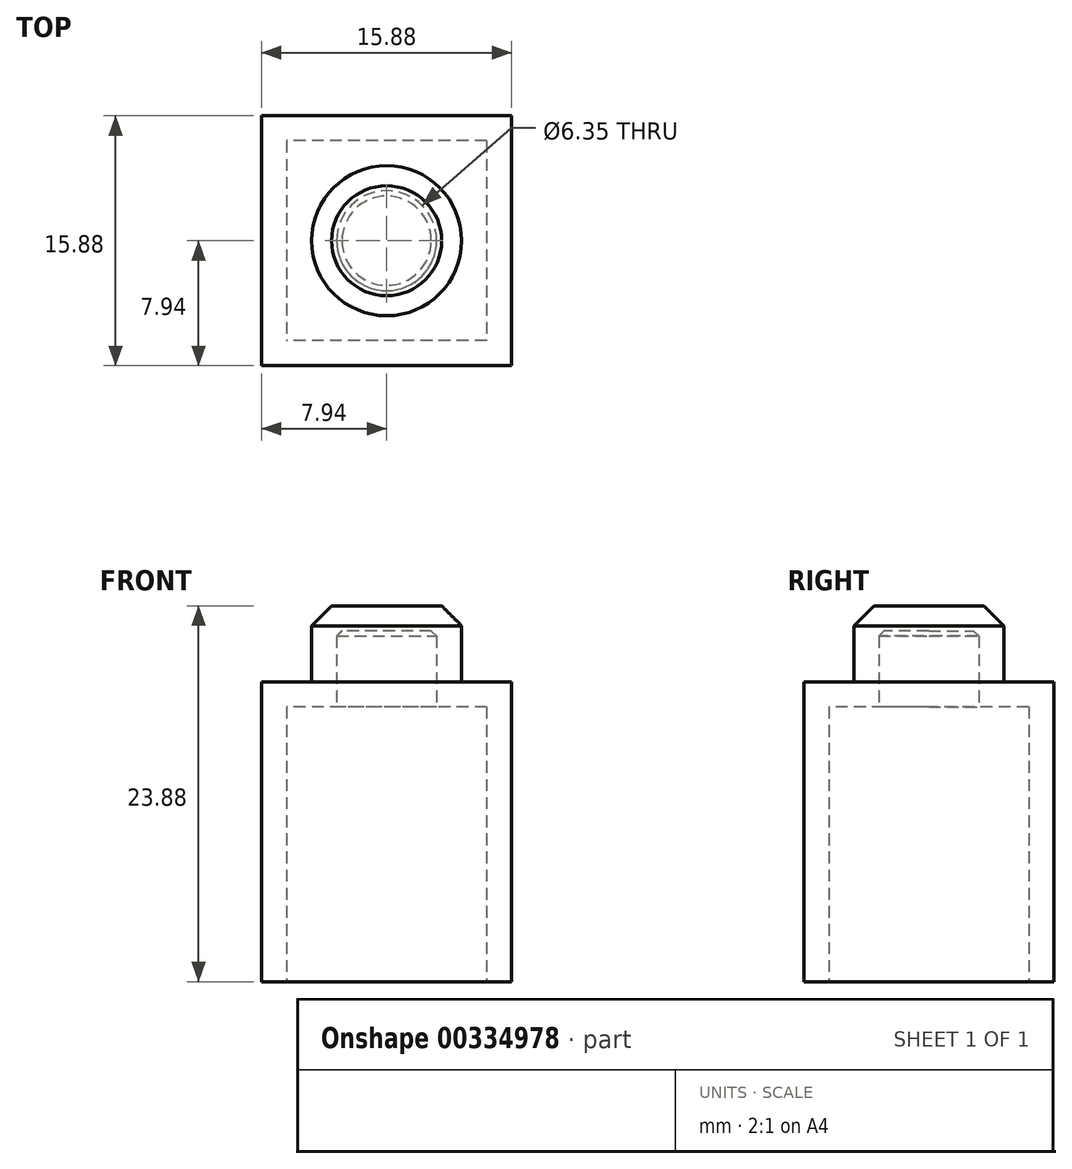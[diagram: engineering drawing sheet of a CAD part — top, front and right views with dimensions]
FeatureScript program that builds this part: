
annotation { "Feature Type Name" : "Feature", "Feature Type Description" : "" }
export const myFeature = defineFeature(function(context is Context, id is Id, definition is map)
    precondition{}
    {
        {
            var Q0;
            Q0=qCreatedBy(makeId("Top.planeOp"),FACE);
            var sketch = newSketch(context, id + "F0", { "sketchPlane" : qUnion([Q0])});
            skLineSegment(sketch, "E0.bottom", {"start": v(7.94, 7.94) * mm, "end": v(-7.94, 7.94) * mm});
            skLineSegment(sketch, "E0.top", {"start": v(7.94, -7.94) * mm, "end": v(-7.94, -7.94) * mm});
            skLineSegment(sketch, "E0.left", {"start": v(7.94, 7.94) * mm, "end": v(7.94, -7.94) * mm});
            skLineSegment(sketch, "E0.right", {"start": v(-7.94, 7.94) * mm, "end": v(-7.94, -7.94) * mm});
            skPoint(sketch, "E0.middle", {"position": v(0, 0) * mm});
            skSolve(sketch);
        }
        {
            var Q0;
            Q0 = qSketchRegion(id + "F0", true);
            extrude(context, id + "F1", {"entities" : qUnion([Q0]), "endBound" : BoundingType.SYMMETRIC, "depth" : 19.05 * mm});
        }
        {
            var Q0;
            Q0=makeQuery(id+"F1.opExtrude","CAP_FACE",FACE,{"disambiguationData":[OSD([sQuery(id+"F0.wireOp",EDGE,"E0.bottom"),sQuery(id+"F0.wireOp",EDGE,"E0.top"),sQuery(id+"F0.wireOp",EDGE,"E0.left"),sQuery(id+"F0.wireOp",EDGE,"E0.right")])],"isStart":false});
            var sketch = newSketch(context, id + "F2", { "sketchPlane" : qUnion([Q0])});
            skCircle(sketch, "E1", {"center": v(0, 0) * mm, "radius": 4.76 * mm});
            skSolve(sketch);
        }
        {
            var Q0;
            Q0 = qSketchRegion(id + "F2", true);
            extrude(context, id + "F3", {"entities" : qUnion([Q0]), "operationType" : NewBodyOperationType.ADD, "depth" : 4.83 * mm});
        }
        {
            var Q0;
            Q0=makeQuery(id+"F3.opExtrude","CAP_EDGE",EDGE,{"disambiguationData":[OSD([sQuery(id+"F2.wireOp",EDGE,"E1")])],"isStart":false});
            chamfer(context, id + "F4", {"entities" : qUnion([Q0]), "width" : 1.27 * mm, "tangentPropagation" : true});
        }
        {
            var Q0;
            Q0=makeQuery(id+"F1.opExtrude","CAP_FACE",FACE,{"disambiguationData":[OSD([sQuery(id+"F0.wireOp",EDGE,"E0.bottom"),sQuery(id+"F0.wireOp",EDGE,"E0.top"),sQuery(id+"F0.wireOp",EDGE,"E0.left"),sQuery(id+"F0.wireOp",EDGE,"E0.right")])],"isStart":true});
            shell(context, id + "F5", {"entities" : qUnion([Q0]), "thickness" : 1.59 * mm});
        }
    });
